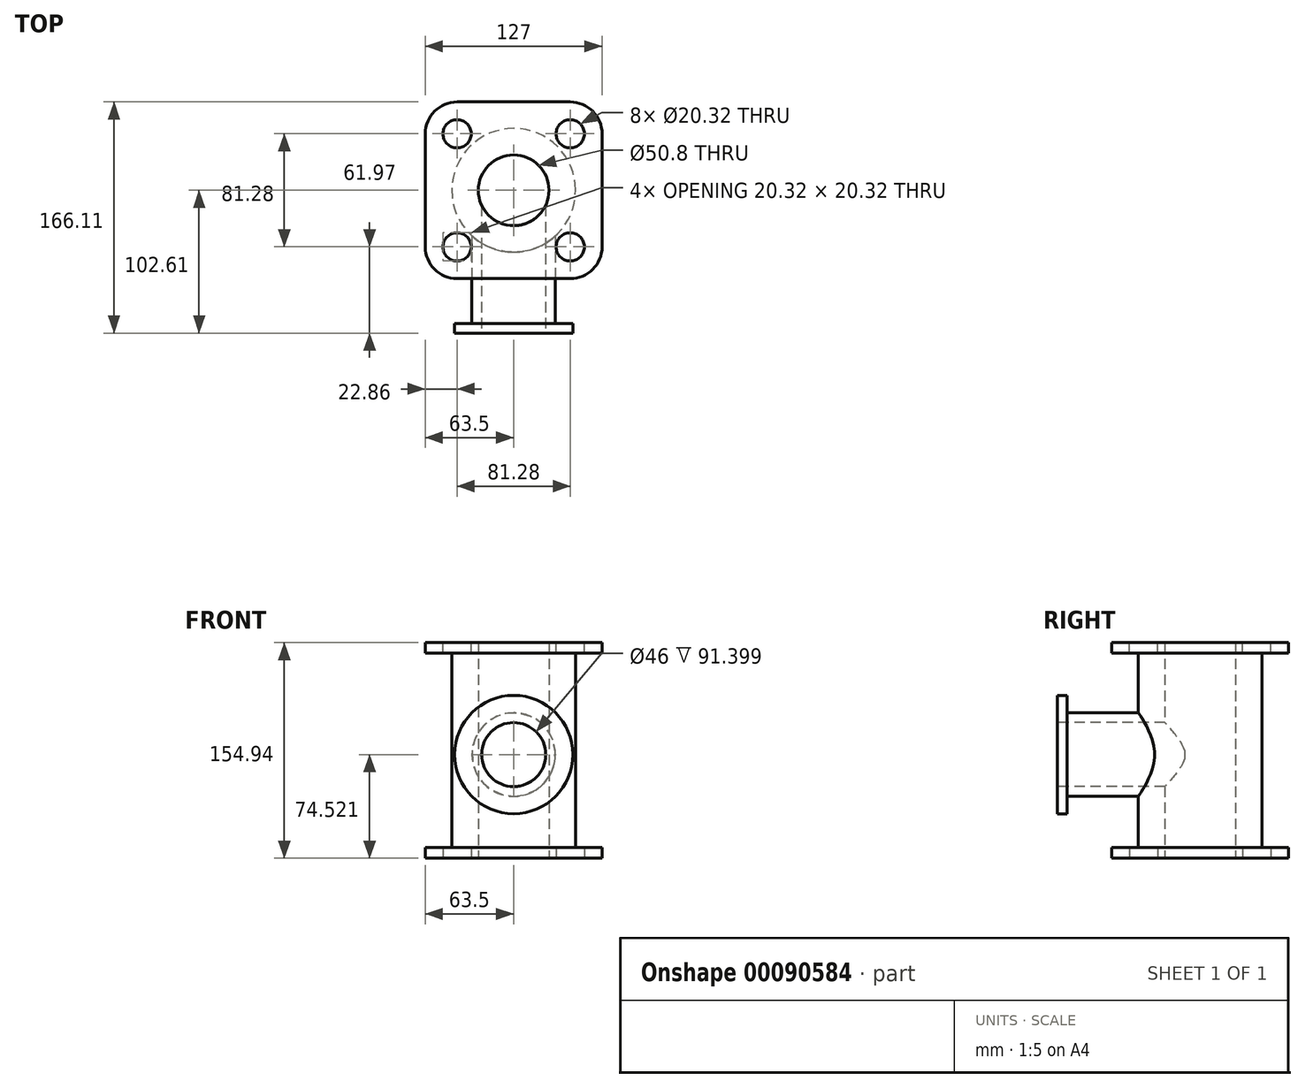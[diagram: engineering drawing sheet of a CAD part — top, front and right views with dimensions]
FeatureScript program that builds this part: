
annotation { "Feature Type Name" : "Feature", "Feature Type Description" : "" }
export const myFeature = defineFeature(function(context is Context, id is Id, definition is map)
    precondition{}
    {
        {
            var Q0;
            Q0=qCreatedBy(makeId("Top.planeOp"),FACE);
            var sketch = newSketch(context, id + "F0", { "sketchPlane" : qUnion([Q0])});
            skLineSegment(sketch, "E0.bottom", {"start": v(-63.5, 63.5) * mm, "end": v(63.5, 63.5) * mm});
            skLineSegment(sketch, "E0.top", {"start": v(-63.5, -63.5) * mm, "end": v(63.5, -63.5) * mm});
            skLineSegment(sketch, "E0.left", {"start": v(-63.5, 63.5) * mm, "end": v(-63.5, -63.5) * mm});
            skLineSegment(sketch, "E0.right", {"start": v(63.5, 63.5) * mm, "end": v(63.5, -63.5) * mm});
            skPoint(sketch, "E0.middle", {"position": v(0, 0) * mm});
            skSolve(sketch);
        }
        {
            var Q0;
            Q0=makeQuery(id+"F0.imprint","IMPRINT",FACE,{"disambiguationData":[TD([[makeQuery(id+"F0.imprint","IMPRINT",EDGE,{"derivedFrom":sQuery(id+"F0.wireOp",EDGE,"E0.bottom")}),-1.0]])]});
            extrude(context, id + "F1", {"entities" : qUnion([Q0]), "depth" : 7.62 * mm});
        }
        {
            var Q0;
            Q0=makeQuery(id+"F1.opExtrude","CAP_FACE",FACE,{"disambiguationData":[OSD([sQuery(id+"F0.wireOp",EDGE,"E0.bottom"),sQuery(id+"F0.wireOp",EDGE,"E0.top"),sQuery(id+"F0.wireOp",EDGE,"E0.left"),sQuery(id+"F0.wireOp",EDGE,"E0.right")])],"isStart":false});
            var sketch = newSketch(context, id + "F2", { "sketchPlane" : qUnion([Q0])});
            skCircle(sketch, "E1", {"center": v(0, 0) * mm, "radius": 44.45 * mm});
            skSolve(sketch);
        }
        {
            var Q0;
            Q0=makeQuery(id+"F2.imprint","IMPRINT",FACE,{"disambiguationData":[TD([[makeQuery(id+"F2.imprint","IMPRINT",EDGE,{"derivedFrom":sQuery(id+"F2.wireOp",EDGE,"E1")}),1.0]])]});
            extrude(context, id + "F3", {"entities" : qUnion([Q0]), "operationType" : NewBodyOperationType.ADD, "depth" : 139.7 * mm});
        }
        {
            var Q0;
            Q0=makeQuery(id+"F1.opExtrude","SWEPT_EDGE",EDGE,{"disambiguationData":[OSD([sQuery(id+"F0.wireOp",EDGE,"E0.top"),sQuery(id+"F0.wireOp",EDGE,"E0.right")])]});
            var Q1;
            Q1=makeQuery(id+"F1.opExtrude","SWEPT_EDGE",EDGE,{"disambiguationData":[OSD([sQuery(id+"F0.wireOp",EDGE,"E0.bottom"),sQuery(id+"F0.wireOp",EDGE,"E0.right")])]});
            var Q2;
            Q2=makeQuery(id+"F1.opExtrude","SWEPT_EDGE",EDGE,{"disambiguationData":[OSD([sQuery(id+"F0.wireOp",EDGE,"E0.top"),sQuery(id+"F0.wireOp",EDGE,"E0.left")])]});
            var Q3;
            Q3=makeQuery(id+"F1.opExtrude","SWEPT_EDGE",EDGE,{"disambiguationData":[OSD([sQuery(id+"F0.wireOp",EDGE,"E0.bottom"),sQuery(id+"F0.wireOp",EDGE,"E0.left")])]});
            fillet(context, id + "F4", {"entities" : qUnion([Q0, Q1, Q2, Q3]), "radius" : 22.86 * mm, "tangentPropagation" : true, "allowEdgeOverflow" : false});
        }
        {
            var Q0;
            Q0=qCreatedBy(makeId("Top.planeOp"),FACE);
            cPlane(context, id + "F5", {"entities" : qUnion([Q0]), "cplaneType" : CPlaneType.OFFSET, "offset" : 77.47 * mm, "width" : 152.4 * mm, "height" : 152.4 * mm});
        }
        {
            var Q0;
            Q0=makeQuery(id+"F1.opExtrude","CAP_FACE",FACE,{"disambiguationData":[OSD([sQuery(id+"F0.wireOp",EDGE,"E0.bottom"),sQuery(id+"F0.wireOp",EDGE,"E0.top"),sQuery(id+"F0.wireOp",EDGE,"E0.left"),sQuery(id+"F0.wireOp",EDGE,"E0.right")])],"isStart":true});
            var sketch = newSketch(context, id + "F6", { "sketchPlane" : qUnion([Q0])});
            skCircle(sketch, "E2", {"center": v(40.64, -40.64) * mm, "radius": 10.16 * mm});
            skCircle(sketch, "E3.MirrorC", {"center": v(-40.64, -40.64) * mm, "radius": 10.16 * mm});
            skCircle(sketch, "E4.MirrorC", {"center": v(40.64, 40.64) * mm, "radius": 10.16 * mm});
            skCircle(sketch, "E5.MirrorC", {"center": v(-40.64, 40.64) * mm, "radius": 10.16 * mm});
            skSolve(sketch);
        }
        {
            var Q0;
            Q0 = qSketchRegion(id + "F6", true);
            extrude(context, id + "F7", {"entities" : qUnion([Q0]), "operationType" : NewBodyOperationType.REMOVE, "oppositeDirection" : true, "depth" : 25.4 * mm});
        }
        {
            var Q0;
            Q0=makeQuery(id+"F1.opExtrude","SWEPT_BODY",BODY,{"disambiguationData":[OSD([sQuery(id+"F0.wireOp",EDGE,"E0.bottom"),sQuery(id+"F0.wireOp",EDGE,"E0.top"),sQuery(id+"F0.wireOp",EDGE,"E0.left"),sQuery(id+"F0.wireOp",EDGE,"E0.right")])]});
            var Q1;
            Q1=qCreatedBy(id+"F5.planeOp",FACE);
            mirror(context, id + "F8", {"operationType" : NewBodyOperationType.ADD, "entities" : qUnion([Q0]), "mirrorPlane" : qUnion([Q1])});
        }
        {
            var Q0;
            Q0=makeQuery(id+"F1.opExtrude","CAP_FACE",FACE,{"disambiguationData":[OSD([sQuery(id+"F0.wireOp",EDGE,"E0.bottom"),sQuery(id+"F0.wireOp",EDGE,"E0.top"),sQuery(id+"F0.wireOp",EDGE,"E0.left"),sQuery(id+"F0.wireOp",EDGE,"E0.right")])],"isStart":true});
            var sketch = newSketch(context, id + "F9", { "sketchPlane" : qUnion([Q0])});
            skCircle(sketch, "E6", {"center": v(0, 0) * mm, "radius": 25.4 * mm});
            skSolve(sketch);
        }
        {
            var Q0;
            Q0=makeQuery(id+"F9.imprint","IMPRINT",FACE,{"disambiguationData":[TD([[makeQuery(id+"F9.imprint","IMPRINT",EDGE,{"derivedFrom":sQuery(id+"F9.wireOp",EDGE,"E6")}),1.0]])]});
            extrude(context, id + "F10", {"entities" : qUnion([Q0]), "operationType" : NewBodyOperationType.REMOVE, "endBound" : BoundingType.THROUGH_ALL, "oppositeDirection" : true, "depth" : 25.4 * mm});
        }
        {
            var Q0;
            Q0=qCreatedBy(makeId("Front.planeOp"),FACE);
            cPlane(context, id + "F11", {"entities" : qUnion([Q0]), "cplaneType" : CPlaneType.OFFSET, "offset" : 44.45 * mm, "width" : 152.4 * mm, "height" : 152.4 * mm});
        }
        {
            var Q0;
            Q0=qCreatedBy(id+"F11.planeOp",FACE);
            var sketch = newSketch(context, id + "F12", { "sketchPlane" : qUnion([Q0])});
            skCircle(sketch, "E7", {"center": v(0, 74.52) * mm, "radius": 30 * mm});
            skSolve(sketch);
        }
        {
            var Q0;
            Q0=makeQuery(id+"F12.imprint","IMPRINT",FACE,{"disambiguationData":[TD([[makeQuery(id+"F12.imprint","IMPRINT",EDGE,{"derivedFrom":sQuery(id+"F12.wireOp",EDGE,"E7")}),1.0]])]});
            extrude(context, id + "F13", {"entities" : qUnion([Q0]), "operationType" : NewBodyOperationType.ADD, "endBound" : BoundingType.UP_TO_NEXT, "oppositeDirection" : true, "depth" : 25 * mm, "hasSecondDirection" : true, "secondDirectionOppositeDirection" : false, "secondDirectionDepth" : 51.16 * mm});
        }
        {
            var Q0;
            Q0=makeQuery(id+"F13.opExtrude","CAP_FACE",FACE,{"disambiguationData":[OSD([sQuery(id+"F12.wireOp",EDGE,"E7")])],"isStart":true});
            var sketch = newSketch(context, id + "F14", { "sketchPlane" : qUnion([Q0])});
            skCircle(sketch, "E8", {"center": v(0, 74.52) * mm, "radius": 42.5 * mm});
            skSolve(sketch);
        }
        {
            var Q0;
            Q0=makeQuery(id+"F14.imprint","IMPRINT",FACE,{"disambiguationData":[TD([[makeQuery(id+"F14.imprint","IMPRINT",EDGE,{"derivedFrom":makeQuery(id+"F13.opExtrude","CAP_EDGE",EDGE,{"disambiguationData":[OSD([sQuery(id+"F12.wireOp",EDGE,"E7")])],"isStart":true})}),1.0]])]});
            var Q1;
            Q1=makeQuery(id+"F14.imprint","IMPRINT",FACE,{"disambiguationData":[TD([[makeQuery(id+"F14.imprint","IMPRINT",EDGE,{"derivedFrom":sQuery(id+"F14.wireOp",EDGE,"E8")}),1.0]])]});
            extrude(context, id + "F15", {"entities" : qUnion([Q0, Q1]), "operationType" : NewBodyOperationType.ADD, "depth" : 7 * mm});
        }
        {
            var Q0;
            Q0=makeQuery(id+"F15.opExtrude","CAP_FACE",FACE,{"disambiguationData":[OSD([sQuery(id+"F14.wireOp",EDGE,"E8")])],"isStart":false});
            var sketch = newSketch(context, id + "F16", { "sketchPlane" : qUnion([Q0])});
            skCircle(sketch, "E9", {"center": v(0, 74.52) * mm, "radius": 23 * mm});
            skSolve(sketch);
        }
        {
            var Q0;
            Q0=makeQuery(id+"F16.imprint","IMPRINT",FACE,{"disambiguationData":[TD([[makeQuery(id+"F16.imprint","IMPRINT",EDGE,{"derivedFrom":sQuery(id+"F16.wireOp",EDGE,"E9")}),1.0]])]});
            extrude(context, id + "F17", {"entities" : qUnion([Q0]), "operationType" : NewBodyOperationType.REMOVE, "oppositeDirection" : true, "depth" : 91.4 * mm});
        }
    });
